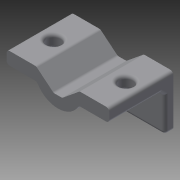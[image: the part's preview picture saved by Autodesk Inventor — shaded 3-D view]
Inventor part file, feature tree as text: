
AUTODESK INVENTOR PART (.ipt)
format: ipt  version: 2014 (Build 180170000, 170)  size: 244,224 bytes
history: native  units: in
note: dims shown in document units (in); Inventor stores cm internally (conversion verified against a paired STEP export)
features: extrude x6, sketch x6, chamfer x1, fillet x1
ambient origin geometry x8: Origin, YZ Plane, XZ Plane, XY Plane, X Axis, Y Axis, Z Axis, Center Point
bodies: Solid1 (feature_tree)
feature tree (14):
  extrude  "Extrusion1"  Depth=0.7874in
  extrude  "Extrusion2"  Depth=0.1575in
  extrude  "Extrusion3"  Depth=0.5906in
  extrude  "Extrusion4"  Depth=0.315in
  extrude  "Extrusion5"  Depth=0.1181in
  extrude  "Extrusion6"  Depth=0.0295in
  chamfer  "Chamfer2"  Distance=0.1319in
  fillet  "Fillet6"  Radius=0.2165in
  sketch  "Sketch1"  dims[d0=0.9843in d1=0.7874in]
  sketch  "Sketch2"  dims[d2=0.1516in d3=0.1575in]
  sketch  "Sketch3"  dims[d4=0.5906in d5=0.7874in]
  sketch  "Sketch4"  dims[d6=0.1969in d7=0.0in d8=0.315in]
  sketch  "Sketch5"  dims[d9=0.0394in d10=0.1181in]
  sketch  "Sketch6"  dims[d11=0.9449in d12=0.0787in d13=0.1319in d14=0.2165in d15=0.0984in d16=0.5906in d17=0.0in d18=0.126in d19=0.5906in d20=0.0in d25=0.3937in d26=0.0in d31=1.0187in d32=1.1344in d33=0.0in d34=0.0in d35=0.0295in d36=0.4724in d37=0.0787in d38=0.0in d39=0.0394in d40=0.0787in d41=45.0deg]
